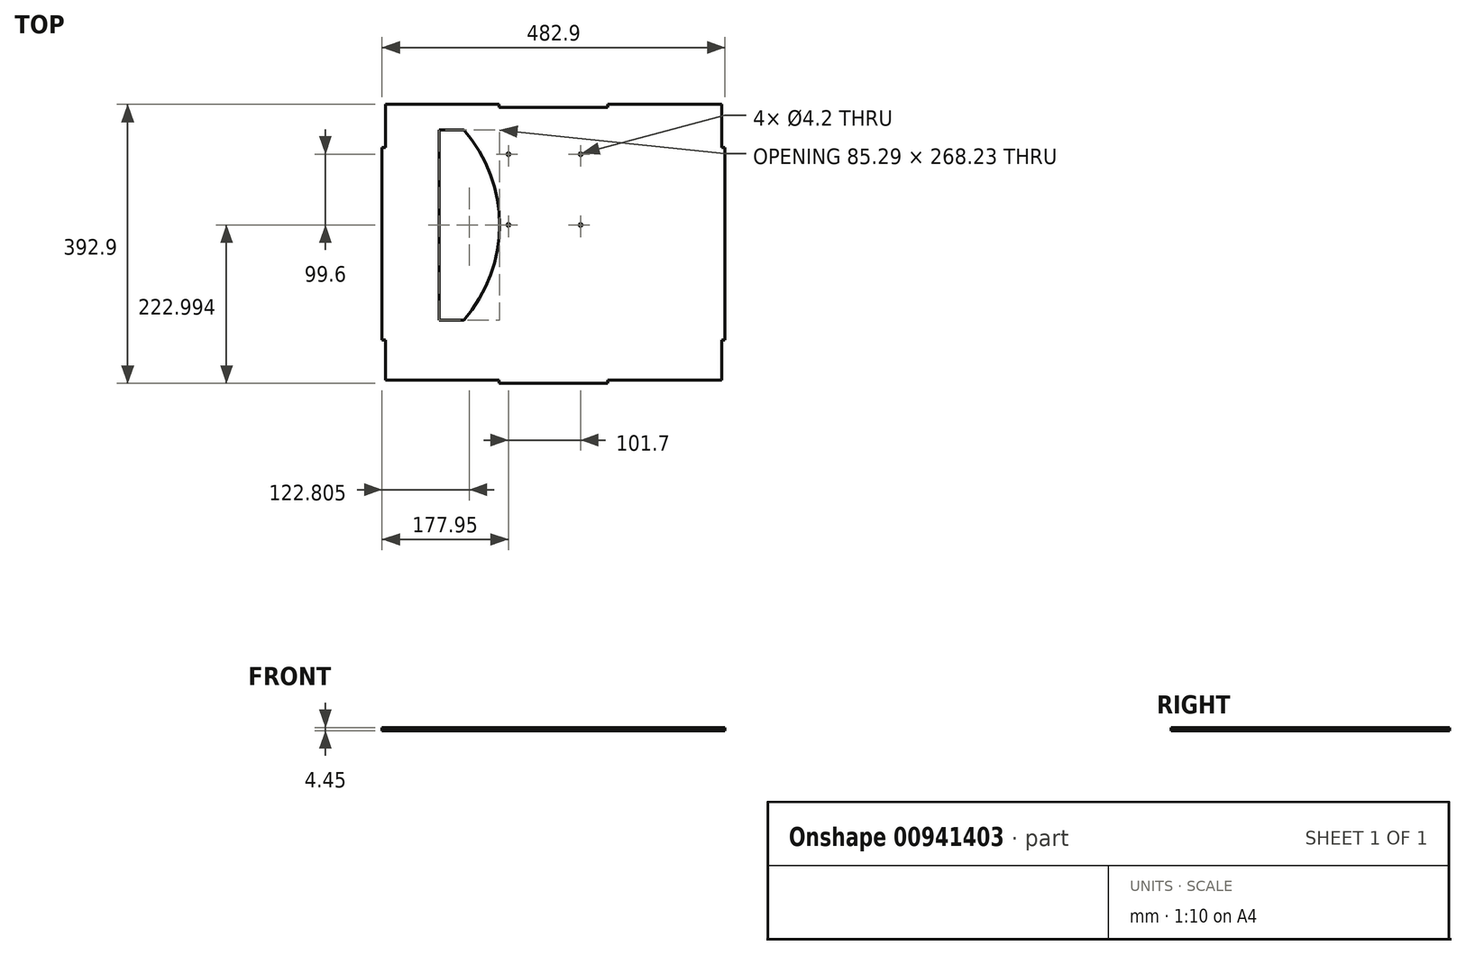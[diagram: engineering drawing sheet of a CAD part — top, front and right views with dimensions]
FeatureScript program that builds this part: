
annotation { "Feature Type Name" : "Feature", "Feature Type Description" : "" }
export const myFeature = defineFeature(function(context is Context, id is Id, definition is map)
    precondition{}
    {
        {
            var Q0;
            Q0=qCreatedBy(makeId("Top.planeOp"),FACE);
            var sketch = newSketch(context, id + "F0", { "sketchPlane" : qUnion([Q0])});
            skPoint(sketch, "E0.middle", {"position": v(0, -13.55) * mm});
            skLineSegment(sketch, "E1.bottom", {"start": v(237, -205.55) * mm, "end": v(76.58, -205.55) * mm});
            skLineSegment(sketch, "E1.top", {"start": v(76.58, 178.45) * mm, "end": v(-76.58, 178.45) * mm});
            skLineSegment(sketch, "E1.left", {"start": v(237, -205.55) * mm, "end": v(237, -149.3) * mm});
            skLineSegment(sketch, "E1.right", {"start": v(-237, -205.55) * mm, "end": v(-237, -149.3) * mm});
            skLineSegment(sketch, "E2.top", {"start": v(-237, 182.9) * mm, "end": v(-76.58, 182.9) * mm});
            skLineSegment(sketch, "E2.left", {"start": v(-237, 178.45) * mm, "end": v(-237, 182.9) * mm});
            skLineSegment(sketch, "E2.right", {"start": v(-76.58, 178.45) * mm, "end": v(-76.58, 182.9) * mm});
            skLineSegment(sketch, "E3.MirrorCS", {"start": v(76.58, 178.45) * mm, "end": v(76.58, 182.9) * mm});
            skLineSegment(sketch, "E4.MirrorCS", {"start": v(237, 182.9) * mm, "end": v(76.58, 182.9) * mm});
            skLineSegment(sketch, "E5.MirrorCS", {"start": v(237, 178.45) * mm, "end": v(237, 182.9) * mm});
            skLineSegment(sketch, "E6.top", {"start": v(-76.58, -210) * mm, "end": v(76.58, -210) * mm});
            skLineSegment(sketch, "E6.left", {"start": v(-76.58, -205.55) * mm, "end": v(-76.58, -210) * mm});
            skLineSegment(sketch, "E6.right", {"start": v(76.58, -205.55) * mm, "end": v(76.58, -210) * mm});
            skLineSegment(sketch, "E7.trimOffspring", {"start": v(-76.58, -205.55) * mm, "end": v(-237, -205.55) * mm});
            skLineSegment(sketch, "E8.bottom", {"start": v(241.45, -149.3) * mm, "end": v(237, -149.3) * mm});
            skLineSegment(sketch, "E8.top", {"start": v(241.45, 122.2) * mm, "end": v(237, 122.2) * mm});
            skLineSegment(sketch, "E8.left", {"start": v(241.45, -149.3) * mm, "end": v(241.45, 122.2) * mm});
            skLineSegment(sketch, "E8.right", {"start": v(-241.45, -149.3) * mm, "end": v(-241.45, 122.2) * mm});
            skLineSegment(sketch, "E9.trimOffspring", {"start": v(-237, 122.2) * mm, "end": v(-241.45, 122.2) * mm});
            skLineSegment(sketch, "E10.trimOffspring", {"start": v(-237, -149.3) * mm, "end": v(-241.45, -149.3) * mm});
            skLineSegment(sketch, "E11.trimOffspring", {"start": v(-237, 122.2) * mm, "end": v(-237, 178.45) * mm});
            skLineSegment(sketch, "E12.trimOffspring", {"start": v(237, 122.2) * mm, "end": v(237, 178.45) * mm});
            skLineSegment(sketch, "E13", {"start": v(40.3, 112.6) * mm, "end": v(38.2, 112.6) * mm});
            skLineSegment(sketch, "E14", {"start": v(38.2, 112.6) * mm, "end": v(38.2, 110.5) * mm});
            skLineSegment(sketch, "E15", {"start": v(38.2, 112.6) * mm, "end": v(36.1, 112.6) * mm});
            skLineSegment(sketch, "E16", {"start": v(38.2, 13) * mm, "end": v(36.1, 13) * mm});
            skLineSegment(sketch, "E17", {"start": v(-63.5, 110.5) * mm, "end": v(-63.5, 112.6) * mm});
            skCircle(sketch, "E18", {"center": v(-63.5, 112.6) * mm, "radius": 2.1 * mm});
            skCircle(sketch, "E19", {"center": v(-63.5, 13) * mm, "radius": 2.1 * mm});
            skCircle(sketch, "E20", {"center": v(38.2, 13) * mm, "radius": 2.1 * mm});
            skCircle(sketch, "E21", {"center": v(38.2, 112.6) * mm, "radius": 2.1 * mm});
            skLineSegment(sketch, "E22.trimOffspring", {"start": v(38.2, 15.1) * mm, "end": v(38.2, 13) * mm});
            skLineSegment(sketch, "E23.trimOffspring", {"start": v(-61.4, 112.6) * mm, "end": v(-63.5, 112.6) * mm});
            skLineSegment(sketch, "E24.bottom", {"start": v(-126.29, -121.12) * mm, "end": v(-161.29, -121.12) * mm});
            skLineSegment(sketch, "E24.top", {"start": v(-126.29, 147.11) * mm, "end": v(-161.29, 147.11) * mm});
            skLineSegment(sketch, "E24.right", {"start": v(-161.29, -121.12) * mm, "end": v(-161.29, 147.11) * mm});
            skPoint(sketch, "E24.middle", {"position": v(-163.57, 13) * mm});
            skPoint(sketch, "E25.orphan", {"position": v(-161.29, 13) * mm});
            skArc(sketch, "E26", {"start": v(-126.29, -121.12) * mm, "mid": v(-76, 13) * mm, "end": v(-126.29, 147.11) * mm});
            skSolve(sketch);
        }
        {
            var Q0;
            Q0=makeQuery(id+"F0.imprint","IMPRINT",FACE,{"disambiguationData":[TD([[makeQuery(id+"F0.imprint","IMPRINT",EDGE,{"derivedFrom":sQuery(id+"F0.wireOp",EDGE,"E1.bottom")}),-1.0]])]});
            extrude(context, id + "F1", {"entities" : qUnion([Q0]), "depth" : 4.45 * mm, "offsetDistance" : 25 * mm});
        }
    });
